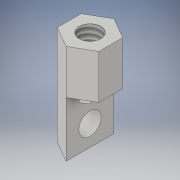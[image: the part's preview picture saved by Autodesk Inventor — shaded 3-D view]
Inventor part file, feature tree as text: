
AUTODESK INVENTOR PART (.ipt)
format: ipt  version: 2018 (Build 220112000, 112)  size: 138,240 bytes
history: native  units: in
note: dims shown in document units (in); Inventor stores cm internally (conversion verified against a paired STEP export)
features: sketch x4, extrude x2, hole x2
ambient origin geometry x8: Origin, YZ Plane, XZ Plane, XY Plane, X Axis, Y Axis, Z Axis, Center Point
bodies: Solid1 (feature_tree)
feature tree (8):
  extrude  "Extrusion1"  TaperAngle=90.0deg  [1 undecoded]
  hole  "Hole1"  [1 undecoded]
  extrude  "Extrusion2"  Depth=0.5in TaperAngle=0.0deg
  hole  "Hole2"  [1 undecoded]
  sketch  "Sketch1"  dims[d0=0.1875in d1=90.0deg]
  sketch  "Sketch2"  dims[d2=2.3622in d4=360.0deg d6=0.9in d7=0.0in]
  sketch  "Sketch3"  dims[d8=0.196in d9=0.25in d10=0.375in d11=0.25in d12=0.5635in d13=0.5in d14=0.8108in d15=0.5in d16=0.0in]
  sketch  "Sketch5"  dims[d17=0.1875in d18=0.266in d19=0.201in d20=0.5in d21=0.507in d22=0.25in d23=0.5635in d24=1.0in d25=0.8108in]
note: 3 required parameter values undecoded (feature->parameter linkage not recoverable at this tier; creation-order binding heuristic only, values carry confidence <= 0.55)
